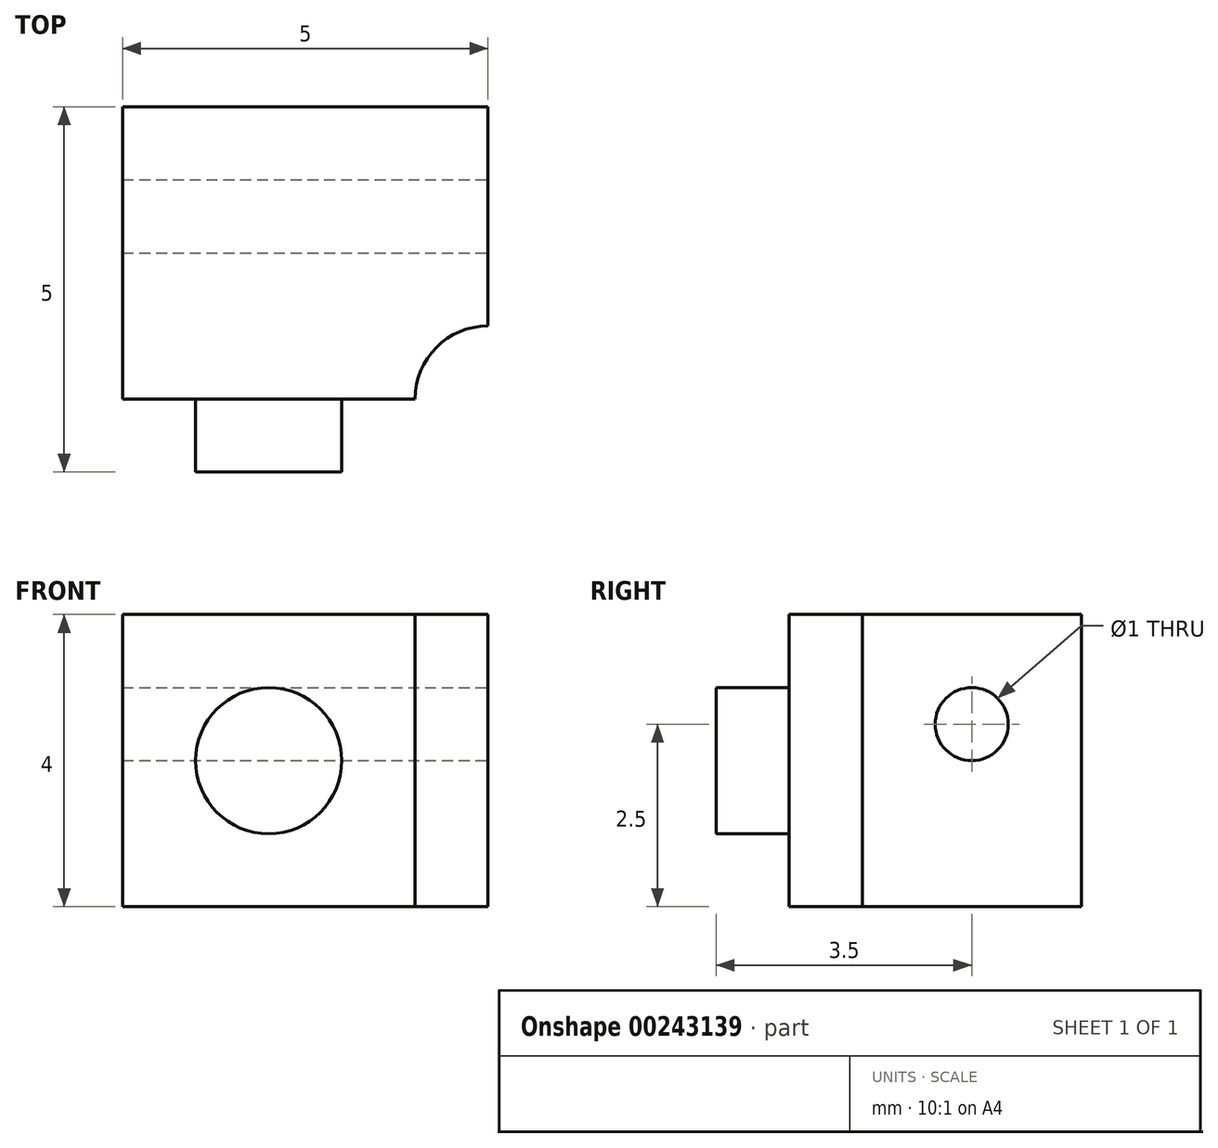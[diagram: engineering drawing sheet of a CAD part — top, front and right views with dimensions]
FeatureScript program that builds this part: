
annotation { "Feature Type Name" : "Feature", "Feature Type Description" : "" }
export const myFeature = defineFeature(function(context is Context, id is Id, definition is map)
    precondition{}
    {
        {
            var Q0;
            Q0=qCreatedBy(makeId("Front.planeOp"),FACE);
            var sketch = newSketch(context, id + "F0", { "sketchPlane" : qUnion([Q0])});
            skLineSegment(sketch, "E0", {"start": v(0, 0) * mm, "end": v(5, 0) * mm});
            skLineSegment(sketch, "E1", {"start": v(5, 0) * mm, "end": v(5, 4) * mm});
            skLineSegment(sketch, "E2", {"start": v(5, 4) * mm, "end": v(0, 4) * mm});
            skLineSegment(sketch, "E3", {"start": v(0, 4) * mm, "end": v(0, 0) * mm});
            skSolve(sketch);
        }
        {
            var Q0;
            Q0 = qSketchRegion(id + "F0", true);
            extrude(context, id + "F1", {"entities" : qUnion([Q0]), "depth" : 4 * mm});
        }
        {
            var Q0;
            Q0=makeQuery(id+"F1.opExtrude","SWEPT_FACE",FACE,{"disambiguationData":[OSD([sQuery(id+"F0.wireOp",EDGE,"E2")])]});
            var sketch = newSketch(context, id + "F2", { "sketchPlane" : qUnion([Q0])});
            skCircle(sketch, "E4", {"center": v(5, -4) * mm, "radius": 1 * mm});
            skSolve(sketch);
        }
        {
            var Q0;
            Q0 = qSketchRegion(id + "F2", true);
            extrude(context, id + "F3", {"entities" : qUnion([Q0]), "operationType" : NewBodyOperationType.REMOVE, "oppositeDirection" : true, "depth" : 4 * mm});
        }
        {
            var Q0;
            Q0=makeQuery(id+"F1.opExtrude","CAP_FACE",FACE,{"disambiguationData":[OSD([sQuery(id+"F0.wireOp",EDGE,"E0"),sQuery(id+"F0.wireOp",EDGE,"E1"),sQuery(id+"F0.wireOp",EDGE,"E2"),sQuery(id+"F0.wireOp",EDGE,"E3")])],"isStart":false});
            var sketch = newSketch(context, id + "F4", { "sketchPlane" : qUnion([Q0])});
            skLineSegment(sketch, "E5", {"start": v(2, 4) * mm, "end": v(2, 0) * mm, "construction": true});
            skCircle(sketch, "E6", {"center": v(2, 2) * mm, "radius": 1 * mm});
            skSolve(sketch);
        }
        {
            var Q0;
            Q0 = qSketchRegion(id + "F4", true);
            extrude(context, id + "F5", {"entities" : qUnion([Q0]), "operationType" : NewBodyOperationType.ADD, "depth" : 1 * mm});
        }
        {
            var Q0;
            Q0=makeQuery(id+"F1.opExtrude","SWEPT_FACE",FACE,{"disambiguationData":[OSD([sQuery(id+"F0.wireOp",EDGE,"E1")])]});
            var sketch = newSketch(context, id + "F6", { "sketchPlane" : qUnion([Q0])});
            skLineSegment(sketch, "E7", {"start": v(-1.5, 4) * mm, "end": v(-1.5, 2.5) * mm, "construction": true});
            skCircle(sketch, "E8", {"center": v(-1.5, 2.5) * mm, "radius": 0.5 * mm});
            skSolve(sketch);
        }
        {
            var Q0;
            Q0 = qSketchRegion(id + "F6", true);
            extrude(context, id + "F7", {"entities" : qUnion([Q0]), "operationType" : NewBodyOperationType.REMOVE, "oppositeDirection" : true, "depth" : 5 * mm});
        }
    });
